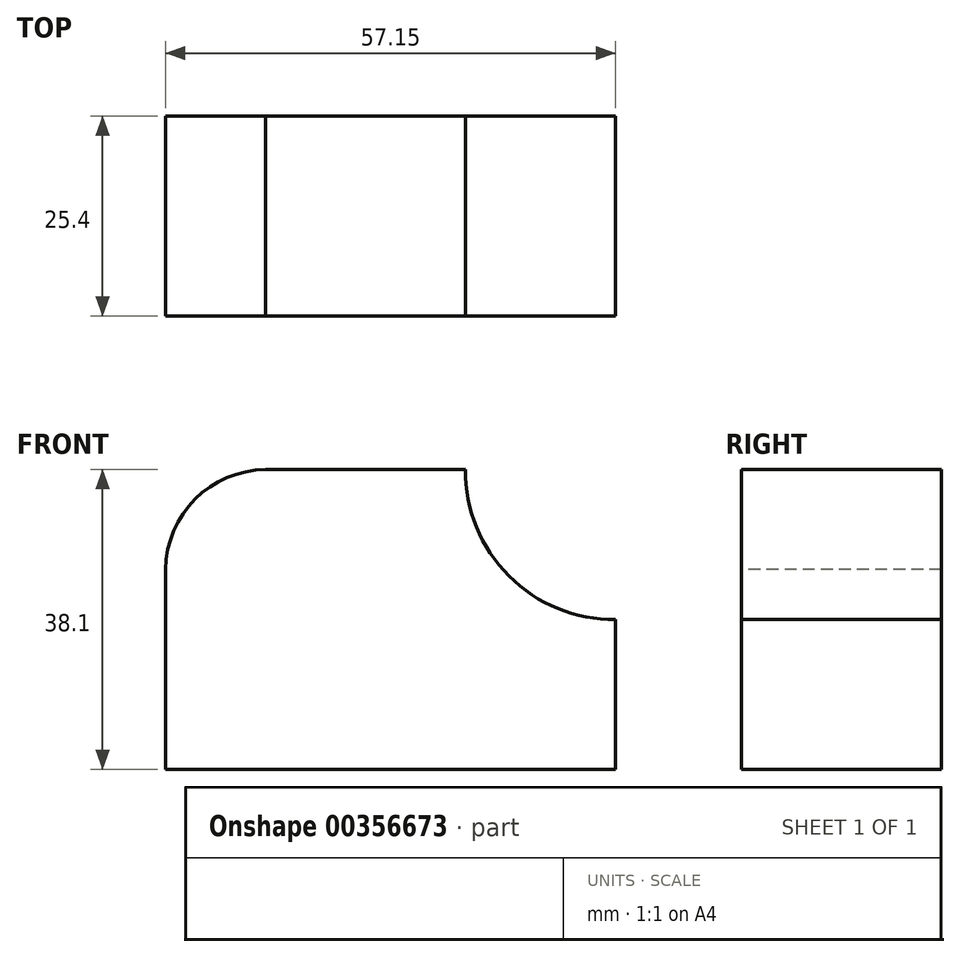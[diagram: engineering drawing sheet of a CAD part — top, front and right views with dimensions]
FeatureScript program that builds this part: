
annotation { "Feature Type Name" : "Feature", "Feature Type Description" : "" }
export const myFeature = defineFeature(function(context is Context, id is Id, definition is map)
    precondition{}
    {
        {
            var Q0;
            Q0=qCreatedBy(makeId("Front.planeOp"),FACE);
            var sketch = newSketch(context, id + "F0", { "sketchPlane" : qUnion([Q0])});
            skLineSegment(sketch, "E0.bottom", {"start": v(0, 0) * mm, "end": v(57.15, 0) * mm});
            skLineSegment(sketch, "E0.top", {"start": v(0, 38.1) * mm, "end": v(57.15, 38.1) * mm});
            skLineSegment(sketch, "E0.left", {"start": v(0, 0) * mm, "end": v(0, 38.1) * mm});
            skLineSegment(sketch, "E0.right", {"start": v(57.15, 0) * mm, "end": v(57.15, 38.1) * mm});
            skSolve(sketch);
        }
        {
            var Q0;
            Q0=makeQuery(id+"F0.imprint","IMPRINT",FACE,{"disambiguationData":[TD([[makeQuery(id+"F0.imprint","IMPRINT",EDGE,{"derivedFrom":sQuery(id+"F0.wireOp",EDGE,"E0.bottom")}),1.0]])]});
            extrude(context, id + "F1", {"entities" : qUnion([Q0]), "depth" : 25.4 * mm});
        }
        {
            var Q0;
            Q0=makeQuery(id+"F1.opExtrude","CAP_FACE",FACE,{"disambiguationData":[OSD([sQuery(id+"F0.wireOp",EDGE,"E0.bottom"),sQuery(id+"F0.wireOp",EDGE,"E0.top"),sQuery(id+"F0.wireOp",EDGE,"E0.left"),sQuery(id+"F0.wireOp",EDGE,"E0.right")])],"isStart":false});
            var sketch = newSketch(context, id + "F2", { "sketchPlane" : qUnion([Q0])});
            skArc(sketch, "E1", {"start": v(12.7, 38.1) * mm, "mid": v(3.76, 34.34) * mm, "end": v(0, 25.4) * mm});
            skLineSegment(sketch, "E2", {"start": v(12.7, 38.1) * mm, "end": v(0, 38.1) * mm});
            skLineSegment(sketch, "E3", {"start": v(0, 38.1) * mm, "end": v(0, 25.4) * mm});
            skSolve(sketch);
        }
        {
            var Q0;
            Q0=makeQuery(id+"F2.imprint","IMPRINT",FACE,{"disambiguationData":[TD([[makeQuery(id+"F2.imprint","IMPRINT",EDGE,{"derivedFrom":sQuery(id+"F2.wireOp",EDGE,"E1")}),-1.0]])]});
            extrude(context, id + "F3", {"entities" : qUnion([Q0]), "operationType" : NewBodyOperationType.REMOVE, "oppositeDirection" : true, "depth" : 25.4 * mm});
        }
        {
            var Q0;
            Q0=makeQuery(id+"F1.opExtrude","CAP_FACE",FACE,{"disambiguationData":[OSD([sQuery(id+"F0.wireOp",EDGE,"E0.bottom"),sQuery(id+"F0.wireOp",EDGE,"E0.top"),sQuery(id+"F0.wireOp",EDGE,"E0.left"),sQuery(id+"F0.wireOp",EDGE,"E0.right")])],"isStart":false});
            var sketch = newSketch(context, id + "F4", { "sketchPlane" : qUnion([Q0])});
            skArc(sketch, "E4", {"start": v(38.1, 38.1) * mm, "mid": v(43.62, 24.57) * mm, "end": v(57.15, 19.05) * mm});
            skLineSegment(sketch, "E5", {"start": v(57.15, 19.05) * mm, "end": v(57.15, 38.1) * mm});
            skLineSegment(sketch, "E6", {"start": v(57.15, 38.1) * mm, "end": v(38.1, 38.1) * mm});
            skSolve(sketch);
        }
        {
            var Q0;
            Q0=makeQuery(id+"F4.imprint","IMPRINT",FACE,{"disambiguationData":[TD([[makeQuery(id+"F4.imprint","IMPRINT",EDGE,{"derivedFrom":sQuery(id+"F4.wireOp",EDGE,"E4")}),1.0]])]});
            extrude(context, id + "F5", {"entities" : qUnion([Q0]), "operationType" : NewBodyOperationType.REMOVE, "oppositeDirection" : true, "depth" : 25.4 * mm});
        }
    });
